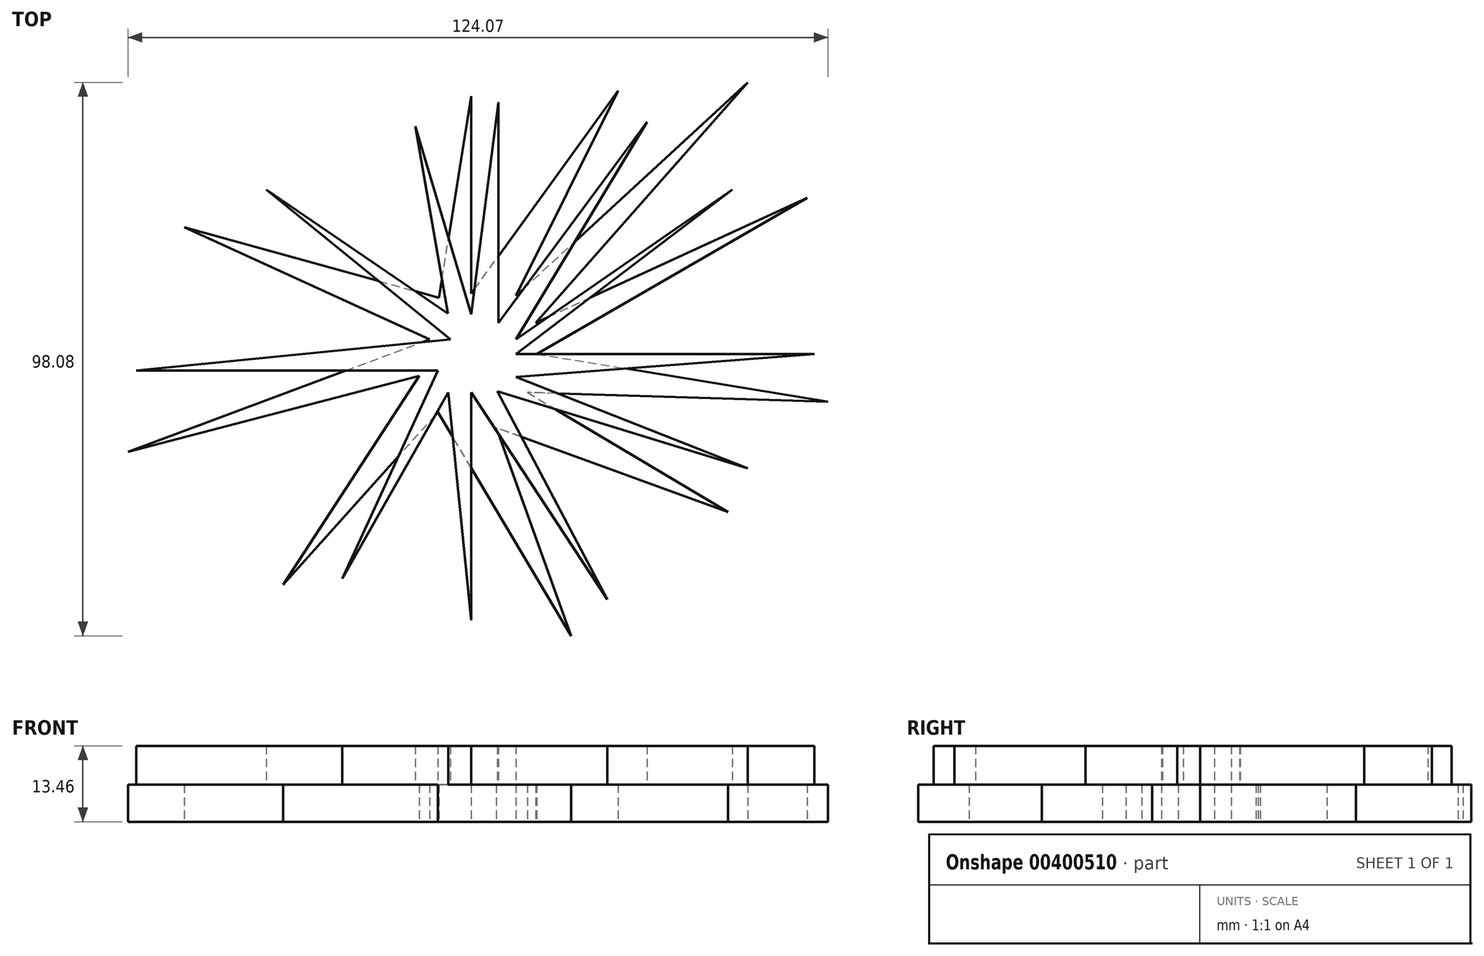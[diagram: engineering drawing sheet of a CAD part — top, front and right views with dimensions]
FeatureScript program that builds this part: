
annotation { "Feature Type Name" : "Feature", "Feature Type Description" : "" }
export const myFeature = defineFeature(function(context is Context, id is Id, definition is map)
    precondition{}
    {
        {
            var Q0;
            Q0=qCreatedBy(makeId("Top.planeOp"),FACE);
            var sketch = newSketch(context, id + "F0", { "sketchPlane" : qUnion([Q0])});
            skLineSegment(sketch, "E0", {"start": v(7.93, 10.32) * mm, "end": v(49.04, 48.12) * mm});
            skLineSegment(sketch, "E1", {"start": v(49.04, 48.12) * mm, "end": v(11.43, 5.53) * mm});
            skLineSegment(sketch, "E2", {"start": v(11.43, 5.53) * mm, "end": v(59.55, 27.65) * mm});
            skLineSegment(sketch, "E3", {"start": v(59.55, 27.65) * mm, "end": v(11.61, 0) * mm});
            skLineSegment(sketch, "E4", {"start": v(11.61, 0) * mm, "end": v(63.23, -8.48) * mm});
            skLineSegment(sketch, "E5", {"start": v(63.23, -8.48) * mm, "end": v(9.96, -6.82) * mm});
            skLineSegment(sketch, "E6", {"start": v(9.96, -6.82) * mm, "end": v(45.54, -28.02) * mm});
            skLineSegment(sketch, "E7", {"start": v(45.54, -28.02) * mm, "end": v(4.42, -13.09) * mm});
            skLineSegment(sketch, "E8", {"start": v(4.42, -13.09) * mm, "end": v(17.7, -49.96) * mm});
            skLineSegment(sketch, "E9", {"start": v(17.7, -49.96) * mm, "end": v(-5.9, -10.32) * mm});
            skLineSegment(sketch, "E10", {"start": v(-5.9, -10.32) * mm, "end": v(-33.37, -40.93) * mm});
            skLineSegment(sketch, "E11", {"start": v(-33.37, -40.93) * mm, "end": v(-9.22, -3.87) * mm});
            skLineSegment(sketch, "E12", {"start": v(-9.22, -3.87) * mm, "end": v(-60.84, -17.33) * mm});
            skLineSegment(sketch, "E13", {"start": v(-60.84, -17.33) * mm, "end": v(-7.37, 2.58) * mm});
            skLineSegment(sketch, "E14", {"start": v(-7.37, 2.58) * mm, "end": v(-50.88, 22.5) * mm});
            skLineSegment(sketch, "E15", {"start": v(-50.88, 22.5) * mm, "end": v(-5.72, 9.96) * mm});
            skLineSegment(sketch, "E16", {"start": v(-5.72, 9.96) * mm, "end": v(0, 45.72) * mm});
            skLineSegment(sketch, "E17", {"start": v(0, 45.72) * mm, "end": v(0, 10.7) * mm});
            skLineSegment(sketch, "E18", {"start": v(0, 10.7) * mm, "end": v(26, 46.64) * mm});
            skLineSegment(sketch, "E19", {"start": v(26, 46.64) * mm, "end": v(7.93, 10.32) * mm});
            skSolve(sketch);
        }
        {
            var Q0;
            Q0 = qSketchRegion(id + "F0", true);
            extrude(context, id + "F1", {"entities" : qUnion([Q0]), "depth" : 6.6 * mm});
        }
        {
            var Q0;
            Q0=makeQuery(id+"F1.opExtrude","CAP_FACE",FACE,{"disambiguationData":[OSD([sQuery(id+"F0.wireOp",EDGE,"E0"),sQuery(id+"F0.wireOp",EDGE,"E1"),sQuery(id+"F0.wireOp",EDGE,"E2"),sQuery(id+"F0.wireOp",EDGE,"E3"),sQuery(id+"F0.wireOp",EDGE,"E4"),sQuery(id+"F0.wireOp",EDGE,"E5"),sQuery(id+"F0.wireOp",EDGE,"E6"),sQuery(id+"F0.wireOp",EDGE,"E7"),sQuery(id+"F0.wireOp",EDGE,"E8"),sQuery(id+"F0.wireOp",EDGE,"E9"),sQuery(id+"F0.wireOp",EDGE,"E10"),sQuery(id+"F0.wireOp",EDGE,"E11"),sQuery(id+"F0.wireOp",EDGE,"E12"),sQuery(id+"F0.wireOp",EDGE,"E13"),sQuery(id+"F0.wireOp",EDGE,"E14"),sQuery(id+"F0.wireOp",EDGE,"E15"),sQuery(id+"F0.wireOp",EDGE,"E16"),sQuery(id+"F0.wireOp",EDGE,"E17"),sQuery(id+"F0.wireOp",EDGE,"E18"),sQuery(id+"F0.wireOp",EDGE,"E19")])],"isStart":false});
            var sketch = newSketch(context, id + "F2", { "sketchPlane" : qUnion([Q0])});
            skLineSegment(sketch, "E20", {"start": v(0, 7) * mm, "end": v(4.8, 44.61) * mm});
            skLineSegment(sketch, "E21", {"start": v(4.8, 44.61) * mm, "end": v(4.8, 5.53) * mm});
            skLineSegment(sketch, "E22", {"start": v(4.8, 5.53) * mm, "end": v(31.16, 41.11) * mm});
            skLineSegment(sketch, "E23", {"start": v(31.16, 41.11) * mm, "end": v(7.93, 2.58) * mm});
            skLineSegment(sketch, "E24", {"start": v(7.93, 2.58) * mm, "end": v(46.27, 29.13) * mm});
            skLineSegment(sketch, "E25", {"start": v(46.27, 29.13) * mm, "end": v(7.93, 0) * mm});
            skLineSegment(sketch, "E26", {"start": v(7.93, 0) * mm, "end": v(60.84, 0) * mm});
            skLineSegment(sketch, "E27", {"start": v(60.84, 0) * mm, "end": v(7.93, -4.06) * mm});
            skLineSegment(sketch, "E28", {"start": v(7.93, -4.06) * mm, "end": v(49.04, -20.28) * mm});
            skLineSegment(sketch, "E29", {"start": v(49.04, -20.28) * mm, "end": v(4.6, -6.64) * mm});
            skLineSegment(sketch, "E30", {"start": v(4.6, -6.64) * mm, "end": v(24.15, -43.5) * mm});
            skLineSegment(sketch, "E31", {"start": v(24.15, -43.5) * mm, "end": v(0, -6.82) * mm});
            skLineSegment(sketch, "E32", {"start": v(0, -6.82) * mm, "end": v(0, -47.2) * mm});
            skLineSegment(sketch, "E33", {"start": v(0, -47.2) * mm, "end": v(-4.06, -6.82) * mm});
            skLineSegment(sketch, "E34", {"start": v(-4.06, -6.82) * mm, "end": v(-22.86, -39.82) * mm});
            skLineSegment(sketch, "E35", {"start": v(-22.86, -39.82) * mm, "end": v(-5.9, -2.95) * mm});
            skLineSegment(sketch, "E36", {"start": v(-5.9, -2.95) * mm, "end": v(-59.36, -2.95) * mm});
            skLineSegment(sketch, "E37", {"start": v(-59.36, -2.95) * mm, "end": v(-3.69, 2.58) * mm});
            skLineSegment(sketch, "E38", {"start": v(-3.69, 2.58) * mm, "end": v(-36.32, 29.13) * mm});
            skLineSegment(sketch, "E39", {"start": v(-36.32, 29.13) * mm, "end": v(-4.15, 7.15) * mm});
            skLineSegment(sketch, "E40", {"start": v(-4.15, 7.15) * mm, "end": v(-9.89, 40.4) * mm});
            skLineSegment(sketch, "E41", {"start": v(-9.89, 40.4) * mm, "end": v(0, 7) * mm});
            skSolve(sketch);
        }
        {
            var Q0;
            Q0 = qSketchRegion(id + "F2", true);
            extrude(context, id + "F3", {"entities" : qUnion([Q0]), "depth" : 6.86 * mm});
        }
    });
